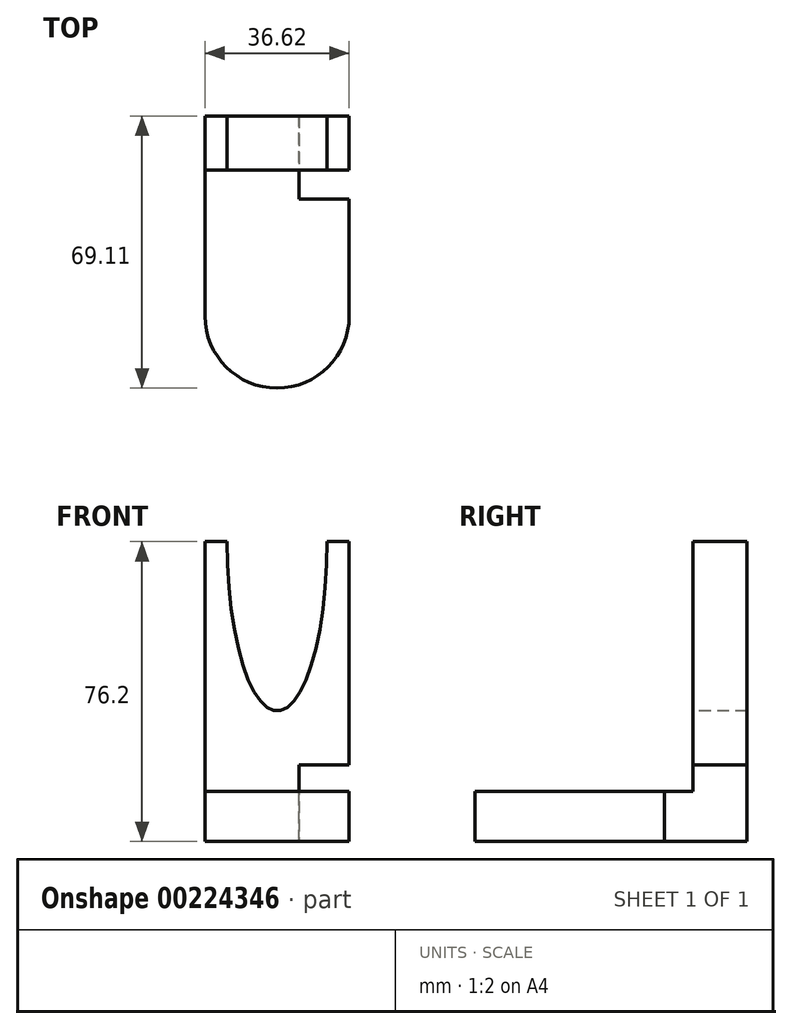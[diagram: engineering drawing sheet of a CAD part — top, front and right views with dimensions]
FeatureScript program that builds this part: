
annotation { "Feature Type Name" : "Feature", "Feature Type Description" : "" }
export const myFeature = defineFeature(function(context is Context, id is Id, definition is map)
    precondition{}
    {
        {
            var Q0;
            Q0=qCreatedBy(makeId("Top.planeOp"),FACE);
            var sketch = newSketch(context, id + "F0", { "sketchPlane" : qUnion([Q0])});
            skLineSegment(sketch, "E0.bottom", {"start": v(-18.31, -25.4) * mm, "end": v(18.31, -25.4) * mm});
            skLineSegment(sketch, "E0.top", {"start": v(-18.31, 25.4) * mm, "end": v(18.31, 25.4) * mm});
            skLineSegment(sketch, "E0.left", {"start": v(-18.31, -25.4) * mm, "end": v(-18.31, 25.4) * mm});
            skLineSegment(sketch, "E0.right", {"start": v(18.31, -25.4) * mm, "end": v(18.31, 25.4) * mm});
            skPoint(sketch, "E0.middle", {"position": v(0, 0) * mm});
            skArc(sketch, "E1", {"start": v(-18.31, -25.4) * mm, "mid": v(0, -43.71) * mm, "end": v(18.31, -25.4) * mm});
            skSolve(sketch);
        }
        {
            var Q0;
            Q0 = qSketchRegion(id + "F0", true);
            extrude(context, id + "F1", {"entities" : qUnion([Q0]), "depth" : 12.7 * mm});
        }
        {
            var Q0;
            Q0=makeQuery(id+"F1.opExtrude","CAP_FACE",FACE,{"disambiguationData":[OSD([sQuery(id+"F0.wireOp",EDGE,"E0.top"),sQuery(id+"F0.wireOp",EDGE,"E0.left"),sQuery(id+"F0.wireOp",EDGE,"E0.right"),sQuery(id+"F0.wireOp",EDGE,"E1")])],"isStart":false});
            var sketch = newSketch(context, id + "F2", { "sketchPlane" : qUnion([Q0])});
            skLineSegment(sketch, "E2.bottom", {"start": v(-18.31, 25.4) * mm, "end": v(18.31, 25.4) * mm});
            skLineSegment(sketch, "E2.top", {"start": v(-18.31, 11.63) * mm, "end": v(18.31, 11.63) * mm});
            skLineSegment(sketch, "E2.left", {"start": v(-18.31, 25.4) * mm, "end": v(-18.31, 11.63) * mm});
            skLineSegment(sketch, "E2.right", {"start": v(18.31, 25.4) * mm, "end": v(18.31, 11.63) * mm});
            skSolve(sketch);
        }
        {
            var Q0;
            Q0 = qSketchRegion(id + "F2", true);
            extrude(context, id + "F3", {"entities" : qUnion([Q0]), "operationType" : NewBodyOperationType.ADD, "depth" : 63.5 * mm});
        }
        {
            var Q0;
            Q0=makeQuery(id+"F3.opExtrude","SWEPT_FACE",FACE,{"disambiguationData":[OSD([sQuery(id+"F2.wireOp",EDGE,"E2.top")])]});
            var sketch = newSketch(context, id + "F4", { "sketchPlane" : qUnion([Q0])});
            skEllipse(sketch, "E3", {"center": v(0, 76.2) * mm, "majorRadius": 43.01 * mm, "minorRadius": 12.7 * mm, "majorAxis": v(0, -1)});
            skSolve(sketch);
        }
        {
            var Q0;
            Q0 = qSketchRegion(id + "F4", true);
            extrude(context, id + "F5", {"entities" : qUnion([Q0]), "operationType" : NewBodyOperationType.REMOVE, "oppositeDirection" : true, "depth" : 15.24 * mm});
        }
        {
            var Q0;
            Q0=makeQuery(id+"F3.boolean.opBoolean","MERGE",FACE,{"derivedFrom":[makeQuery(id+"F1.opExtrude","SWEPT_FACE",FACE,{"disambiguationData":[OSD([sQuery(id+"F0.wireOp",EDGE,"E0.right")])]}),makeQuery(id+"F3.opExtrude","SWEPT_FACE",FACE,{"disambiguationData":[OSD([sQuery(id+"F2.wireOp",EDGE,"E2.right")])]})]});
            var sketch = newSketch(context, id + "F6", { "sketchPlane" : qUnion([Q0])});
            skLineSegment(sketch, "E4.bottom", {"start": v(25.4, 0) * mm, "end": v(4.35, 0) * mm});
            skLineSegment(sketch, "E4.top", {"start": v(25.4, 19.4) * mm, "end": v(4.35, 19.4) * mm});
            skLineSegment(sketch, "E4.left", {"start": v(25.4, 0) * mm, "end": v(25.4, 19.4) * mm});
            skLineSegment(sketch, "E4.right", {"start": v(4.35, 0) * mm, "end": v(4.35, 19.4) * mm});
            skSolve(sketch);
        }
        {
            var Q0;
            Q0 = qSketchRegion(id + "F6", true);
            extrude(context, id + "F7", {"entities" : qUnion([Q0]), "operationType" : NewBodyOperationType.REMOVE, "oppositeDirection" : true, "depth" : 12.7 * mm});
        }
    });
